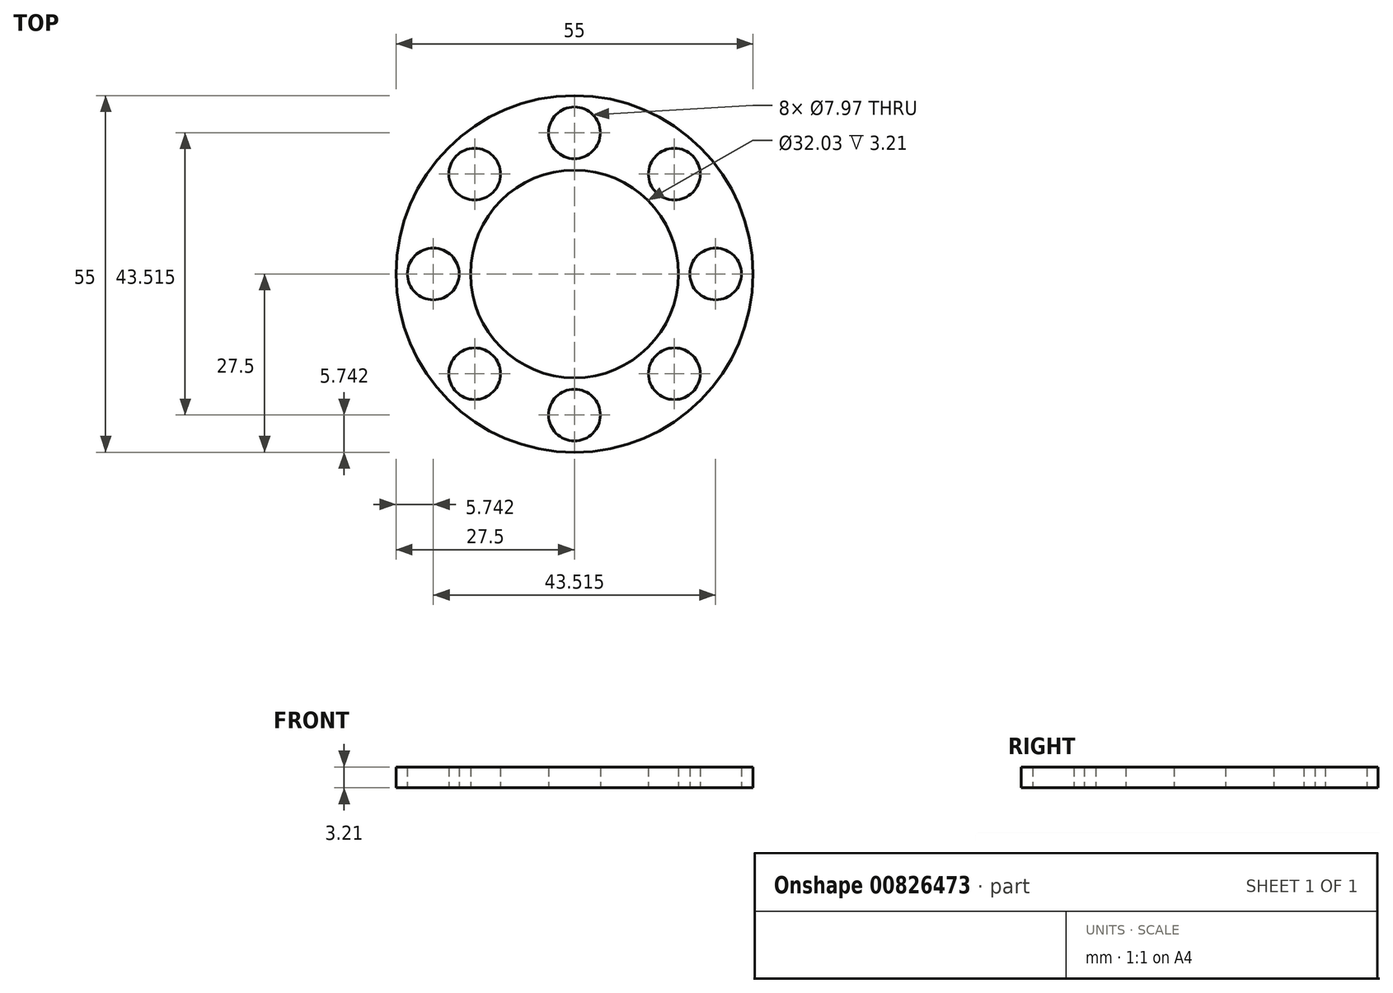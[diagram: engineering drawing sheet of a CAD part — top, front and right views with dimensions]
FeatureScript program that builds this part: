
annotation { "Feature Type Name" : "Feature", "Feature Type Description" : "" }
export const myFeature = defineFeature(function(context is Context, id is Id, definition is map)
    precondition{}
    {
        {
            var Q0;
            Q0=qCreatedBy(makeId("Top.planeOp"),FACE);
            var sketch = newSketch(context, id + "F0", { "sketchPlane" : qUnion([Q0])});
            skCircle(sketch, "E0", {"center": v(0, 0) * mm, "radius": 27.5 * mm});
            skCircle(sketch, "E1", {"center": v(0, 0) * mm, "radius": 16.02 * mm});
            skLineSegment(sketch, "E2", {"start": v(0, 27.5) * mm, "end": v(0, 16.02) * mm, "construction": true});
            skCircle(sketch, "E3", {"center": v(0, 21.76) * mm, "radius": 3.98 * mm});
            skCircle(sketch, "E4.1.0", {"center": v(-15.38, 15.38) * mm, "radius": 3.98 * mm});
            skCircle(sketch, "E4.2.0", {"center": v(-21.76, 0) * mm, "radius": 3.98 * mm});
            skCircle(sketch, "E4.3.0", {"center": v(-15.38, -15.38) * mm, "radius": 3.98 * mm});
            skCircle(sketch, "E4.4.0", {"center": v(0, -21.76) * mm, "radius": 3.98 * mm});
            skCircle(sketch, "E4.5.0", {"center": v(15.38, -15.38) * mm, "radius": 3.98 * mm});
            skCircle(sketch, "E4.6.0", {"center": v(21.76, 0) * mm, "radius": 3.98 * mm});
            skCircle(sketch, "E4.7.0", {"center": v(15.38, 15.38) * mm, "radius": 3.98 * mm});
            skSolve(sketch);
        }
        {
            var Q0;
            Q0=makeQuery(id+"F0.imprint","IMPRINT",FACE,{"disambiguationData":[TD([[makeQuery(id+"F0.imprint","IMPRINT",EDGE,{"derivedFrom":sQuery(id+"F0.wireOp",EDGE,"E0")}),1.0]])]});
            extrude(context, id + "F1", {"entities" : qUnion([Q0]), "depth" : 3.2 * mm, "offsetDistance" : 25 * mm});
        }
    });
